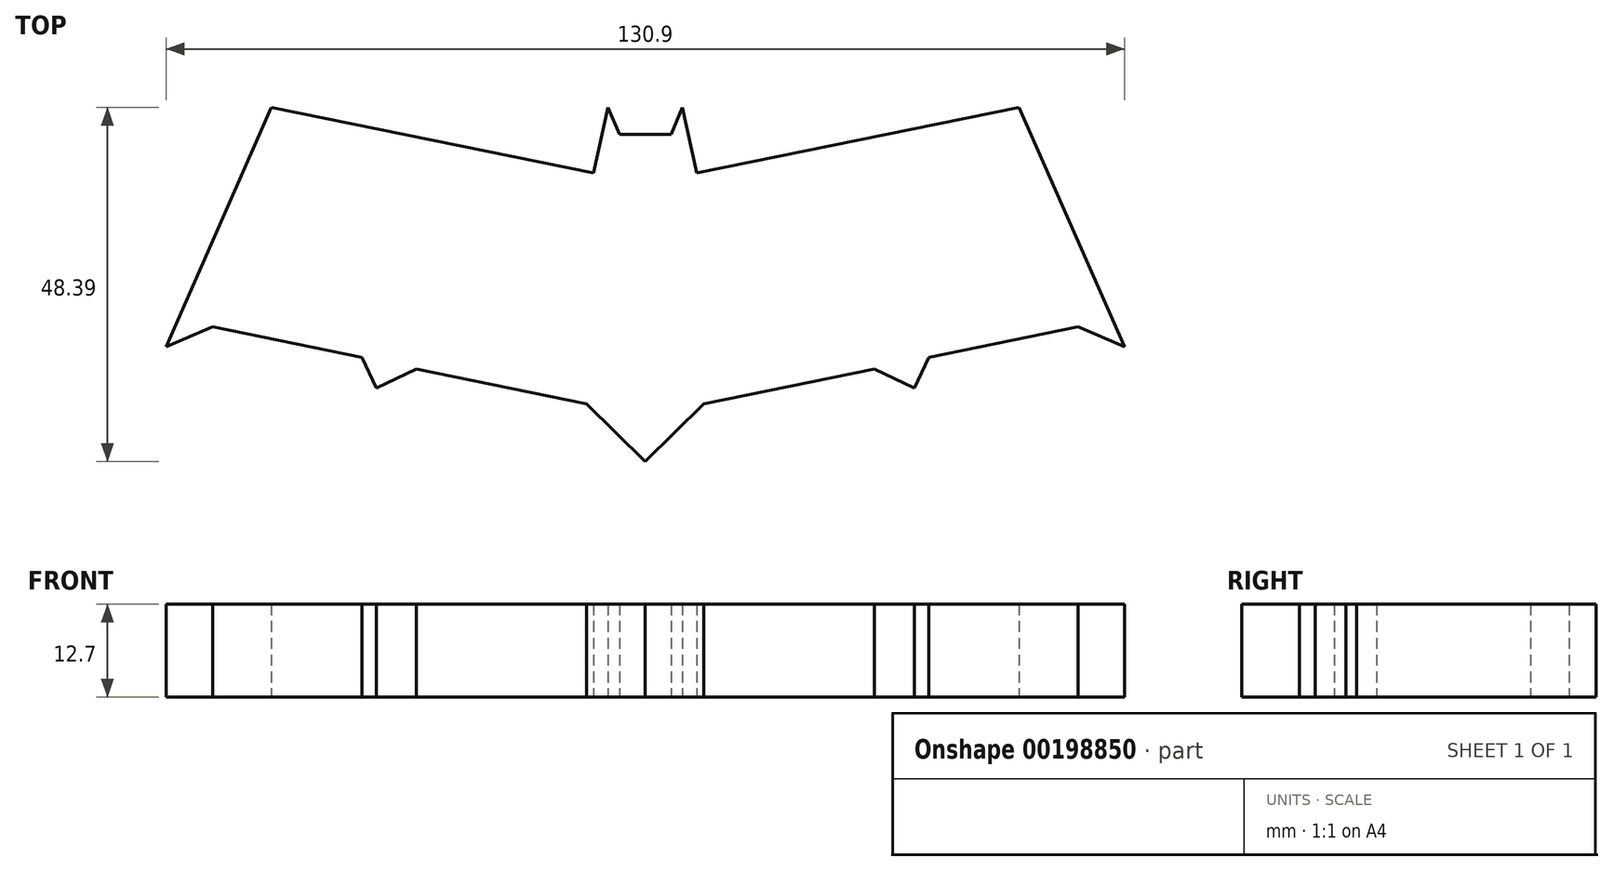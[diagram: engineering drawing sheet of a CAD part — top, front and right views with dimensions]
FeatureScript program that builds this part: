
annotation { "Feature Type Name" : "Feature", "Feature Type Description" : "" }
export const myFeature = defineFeature(function(context is Context, id is Id, definition is map)
    precondition{}
    {
        {
            var Q0;
            Q0=qCreatedBy(makeId("Top.planeOp"),FACE);
            var sketch = newSketch(context, id + "F0", { "sketchPlane" : qUnion([Q0])});
            skLineSegment(sketch, "E0", {"start": v(0, 29.02) * mm, "end": v(0, -15.68) * mm});
            skLineSegment(sketch, "E1", {"start": v(0, 29.02) * mm, "end": v(-3.52, 29.02) * mm});
            skLineSegment(sketch, "E2", {"start": v(-3.52, 29.02) * mm, "end": v(-5.1, 32.7) * mm});
            skLineSegment(sketch, "E3", {"start": v(-5.1, 32.7) * mm, "end": v(-7.03, 23.75) * mm});
            skLineSegment(sketch, "E4", {"start": v(-7.03, 23.75) * mm, "end": v(-51.05, 32.7) * mm});
            skLineSegment(sketch, "E5", {"start": v(-51.05, 32.7) * mm, "end": v(-65.45, 0) * mm});
            skLineSegment(sketch, "E6", {"start": v(-65.45, 0) * mm, "end": v(-59.08, 2.73) * mm});
            skLineSegment(sketch, "E7", {"start": v(-8.01, -7.83) * mm, "end": v(0, -15.68) * mm});
            skLineSegment(sketch, "E8", {"start": v(-38.7, -1.48) * mm, "end": v(-36.72, -5.63) * mm});
            skLineSegment(sketch, "E9", {"start": v(-36.72, -5.63) * mm, "end": v(-31.27, -3.02) * mm});
            skLineSegment(sketch, "E10", {"start": v(-59.08, 2.73) * mm, "end": v(-38.7, -1.48) * mm});
            skLineSegment(sketch, "E11", {"start": v(-31.27, -3.02) * mm, "end": v(-8.01, -7.83) * mm});
            skLineSegment(sketch, "E12.MirrorCS", {"start": v(0, 29.02) * mm, "end": v(3.52, 29.02) * mm});
            skLineSegment(sketch, "E13.MirrorCS", {"start": v(3.52, 29.02) * mm, "end": v(5.1, 32.7) * mm});
            skLineSegment(sketch, "E14.MirrorCS", {"start": v(5.1, 32.7) * mm, "end": v(7.03, 23.75) * mm});
            skLineSegment(sketch, "E15.MirrorCS", {"start": v(7.03, 23.75) * mm, "end": v(51.05, 32.7) * mm});
            skLineSegment(sketch, "E16.MirrorCS", {"start": v(51.05, 32.7) * mm, "end": v(65.45, 0) * mm});
            skLineSegment(sketch, "E17.MirrorCS", {"start": v(65.45, 0) * mm, "end": v(59.08, 2.73) * mm});
            skLineSegment(sketch, "E18.MirrorCS", {"start": v(59.08, 2.73) * mm, "end": v(38.7, -1.48) * mm});
            skLineSegment(sketch, "E19.MirrorCS", {"start": v(38.7, -1.48) * mm, "end": v(36.72, -5.63) * mm});
            skLineSegment(sketch, "E20.MirrorCS", {"start": v(36.72, -5.63) * mm, "end": v(31.27, -3.02) * mm});
            skLineSegment(sketch, "E21.MirrorCS", {"start": v(31.27, -3.02) * mm, "end": v(8.01, -7.83) * mm});
            skLineSegment(sketch, "E22.MirrorCS", {"start": v(8.01, -7.83) * mm, "end": v(0, -15.68) * mm});
            skSolve(sketch);
        }
        {
            var Q0;
            Q0=makeQuery(id+"F0.imprint","IMPRINT",FACE,{"disambiguationData":[TD([[makeQuery(id+"F0.imprint","IMPRINT",EDGE,{"derivedFrom":sQuery(id+"F0.wireOp",EDGE,"E0")}),-1.0]])]});
            var Q1;
            Q1=makeQuery(id+"F0.imprint","IMPRINT",FACE,{"disambiguationData":[TD([[makeQuery(id+"F0.imprint","IMPRINT",EDGE,{"derivedFrom":sQuery(id+"F0.wireOp",EDGE,"E0")}),1.0]])]});
            extrude(context, id + "F1", {"entities" : qUnion([Q0, Q1]), "depth" : 12.7 * mm});
        }
    });
